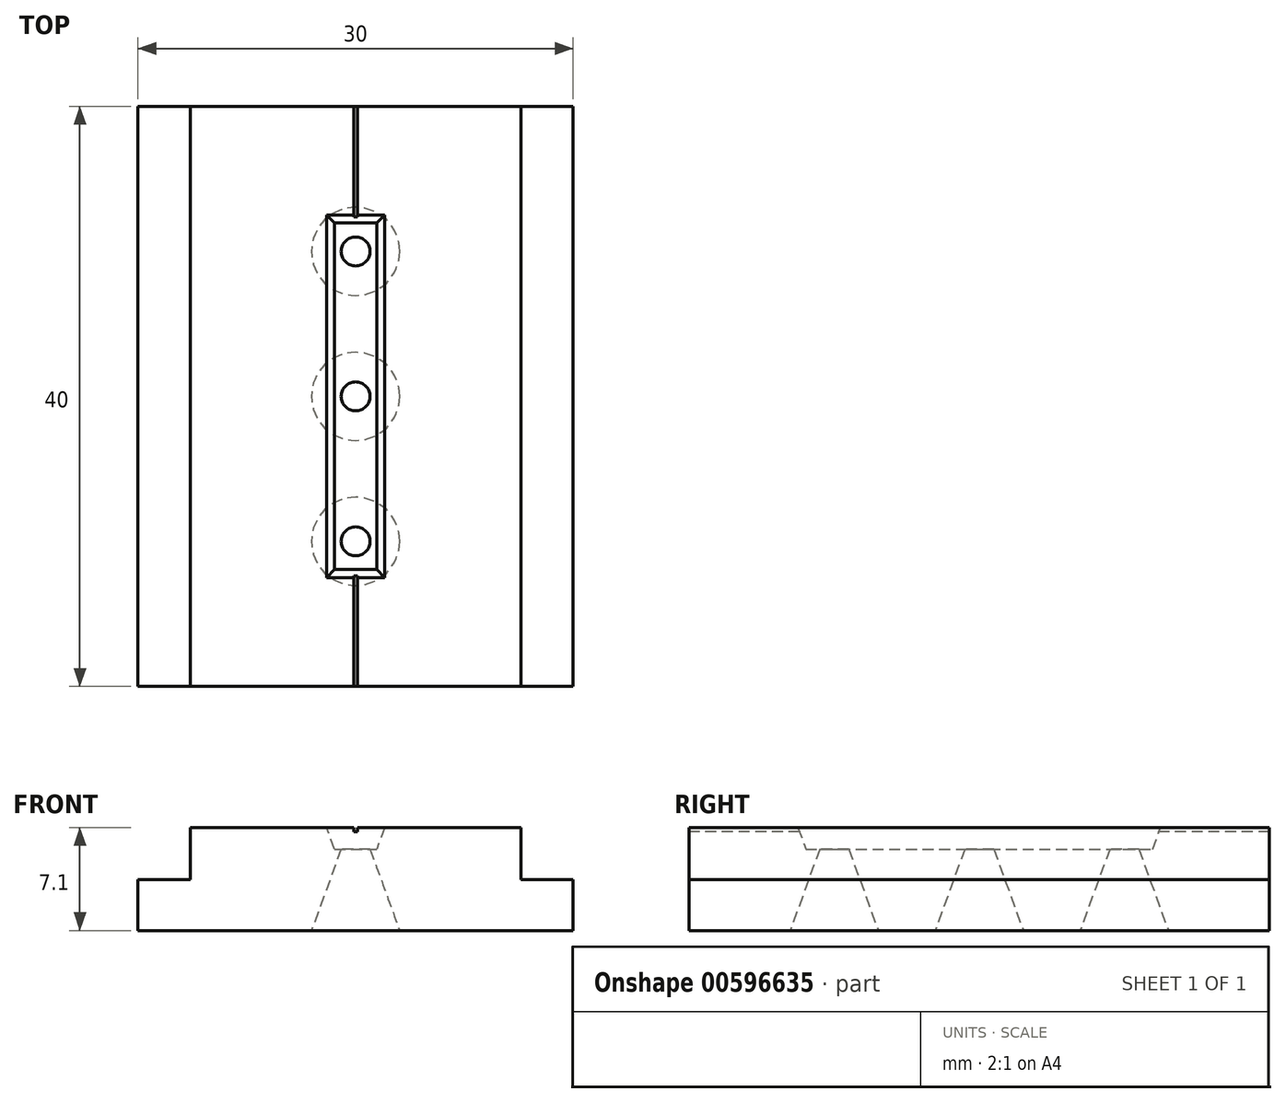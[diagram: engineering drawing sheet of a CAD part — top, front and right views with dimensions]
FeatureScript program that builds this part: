
annotation { "Feature Type Name" : "Feature", "Feature Type Description" : "" }
export const myFeature = defineFeature(function(context is Context, id is Id, definition is map)
    precondition{}
    {
        {
            var Q0;
            Q0=qCreatedBy(makeId("Top.planeOp"),FACE);
            var sketch = newSketch(context, id + "F0", { "sketchPlane" : qUnion([Q0])});
            skLineSegment(sketch, "E0.bottom", {"start": v(0, 0) * mm, "end": v(30, 0) * mm});
            skLineSegment(sketch, "E0.top", {"start": v(0, 40) * mm, "end": v(30, 40) * mm});
            skLineSegment(sketch, "E0.left", {"start": v(0, 0) * mm, "end": v(0, 40) * mm});
            skLineSegment(sketch, "E0.right", {"start": v(30, 0) * mm, "end": v(30, 40) * mm});
            skSolve(sketch);
        }
        {
            var Q0;
            Q0 = qSketchRegion(id + "F0", true);
            extrude(context, id + "F1", {"entities" : qUnion([Q0]), "depth" : (3.5 + 3.6) * mm, "offsetDistance" : 25 * mm});
        }
        {
            var Q0;
            Q0=makeQuery(id+"F1.opExtrude","CAP_FACE",FACE,{"disambiguationData":[OSD([sQuery(id+"F0.wireOp",EDGE,"E0.bottom"),sQuery(id+"F0.wireOp",EDGE,"E0.top"),sQuery(id+"F0.wireOp",EDGE,"E0.left"),sQuery(id+"F0.wireOp",EDGE,"E0.right")])],"isStart":false});
            var sketch = newSketch(context, id + "F2", { "sketchPlane" : qUnion([Q0])});
            skLineSegment(sketch, "E1", {"start": v(15, 40) * mm, "end": v(15, 0) * mm, "construction": true});
            skLineSegment(sketch, "E2", {"start": v(30, 20) * mm, "end": v(0, 20) * mm, "construction": true});
            skLineSegment(sketch, "E3.bottom", {"start": v(17, 7.5) * mm, "end": v(13, 7.5) * mm});
            skLineSegment(sketch, "E3.top", {"start": v(17, 32.5) * mm, "end": v(13, 32.5) * mm});
            skLineSegment(sketch, "E3.left", {"start": v(17, 7.5) * mm, "end": v(17, 32.5) * mm});
            skLineSegment(sketch, "E3.right", {"start": v(13, 7.5) * mm, "end": v(13, 32.5) * mm});
            skPoint(sketch, "E3.middle", {"position": v(15, 20) * mm});
            skSolve(sketch);
        }
        {
            var Q0;
            Q0 = qSketchRegion(id + "F2", true);
            extrude(context, id + "F3", {"entities" : qUnion([Q0]), "operationType" : NewBodyOperationType.REMOVE, "oppositeDirection" : true, "depth" : 1.5 * mm, "offsetDistance" : 25 * mm, "hasDraft" : true, "draftAngle" : 20 * degree, "draftPullDirection" : true});
        }
        {
            var Q0;
            Q0=makeQuery(id+"F1.opExtrude","SWEPT_FACE",FACE,{"disambiguationData":[OSD([sQuery(id+"F0.wireOp",EDGE,"E0.bottom")])]});
            var sketch = newSketch(context, id + "F4", { "sketchPlane" : qUnion([Q0])});
            skLineSegment(sketch, "E4.bottom", {"start": v(0, 3.5) * mm, "end": v(3.6, 3.5) * mm});
            skLineSegment(sketch, "E4.top", {"start": v(0, 7.1) * mm, "end": v(3.6, 7.1) * mm});
            skLineSegment(sketch, "E4.left", {"start": v(0, 3.5) * mm, "end": v(0, 7.1) * mm});
            skLineSegment(sketch, "E4.right", {"start": v(3.6, 3.5) * mm, "end": v(3.6, 7.1) * mm});
            skLineSegment(sketch, "E5", {"start": v(15, 7.1) * mm, "end": v(15, 0) * mm, "construction": true});
            skLineSegment(sketch, "E6", {"start": v(14.88, 7.1) * mm, "end": v(14.88, 6.8) * mm});
            skLineSegment(sketch, "E7", {"start": v(14.88, 6.8) * mm, "end": v(15, 6.8) * mm});
            skLineSegment(sketch, "E8", {"start": v(14.88, 7.1) * mm, "end": v(15, 7.1) * mm});
            skLineSegment(sketch, "E9.MirrorCS", {"start": v(15.12, 7.1) * mm, "end": v(15.12, 6.8) * mm});
            skLineSegment(sketch, "E10.MirrorCS", {"start": v(15.12, 7.1) * mm, "end": v(15, 7.1) * mm});
            skLineSegment(sketch, "E11.MirrorCS", {"start": v(15.12, 6.8) * mm, "end": v(15, 6.8) * mm});
            skLineSegment(sketch, "E12.MirrorCS", {"start": v(30, 3.5) * mm, "end": v(30, 7.1) * mm});
            skLineSegment(sketch, "E13.MirrorCS", {"start": v(30, 7.1) * mm, "end": v(26.4, 7.1) * mm});
            skLineSegment(sketch, "E14.MirrorCS", {"start": v(26.4, 3.5) * mm, "end": v(26.4, 7.1) * mm});
            skLineSegment(sketch, "E15.MirrorCS", {"start": v(30, 3.5) * mm, "end": v(26.4, 3.5) * mm});
            skSolve(sketch);
        }
        {
            var Q0;
            Q0 = qSketchRegion(id + "F4", true);
            extrude(context, id + "F5", {"entities" : qUnion([Q0]), "operationType" : NewBodyOperationType.REMOVE, "endBound" : BoundingType.THROUGH_ALL, "oppositeDirection" : true, "depth" : 25 * mm, "offsetDistance" : 25 * mm});
        }
        {
            var Q0;
            Q0=makeQuery(id+"F3.boolean.opBoolean","COPY",FACE,{"derivedFrom":makeQuery(id+"F3.opExtrude","CAP_FACE",FACE,{"disambiguationData":[OSD([sQuery(id+"F2.wireOp",EDGE,"E3.bottom"),sQuery(id+"F2.wireOp",EDGE,"E3.top"),sQuery(id+"F2.wireOp",EDGE,"E3.left"),sQuery(id+"F2.wireOp",EDGE,"E3.right")])],"isStart":false})});
            var sketch = newSketch(context, id + "F6", { "sketchPlane" : qUnion([Q0])});
            skPoint(sketch, "E16", {"position": v(15, 30) * mm});
            skCircle(sketch, "E17", {"center": v(15, 30) * mm, "radius": 1 * mm});
            skCircle(sketch, "E18.0.1.0", {"center": v(15, 20) * mm, "radius": 1 * mm});
            skCircle(sketch, "E18.0.2.0", {"center": v(15, 10) * mm, "radius": 1 * mm});
            skLineSegment(sketch, "E18.direction1", {"start": v(15, 30) * mm, "end": v(40, 30) * mm, "construction": true});
            skLineSegment(sketch, "E18.direction2", {"start": v(15, 30) * mm, "end": v(15, 20) * mm, "construction": true});
            skSolve(sketch);
        }
        {
            var Q0;
            Q0 = qSketchRegion(id + "F6", true);
            extrude(context, id + "F7", {"entities" : qUnion([Q0]), "operationType" : NewBodyOperationType.REMOVE, "oppositeDirection" : true, "depth" : 20 * mm, "offsetDistance" : 25 * mm, "hasDraft" : true, "draftAngle" : 20 * degree});
        }
    });
